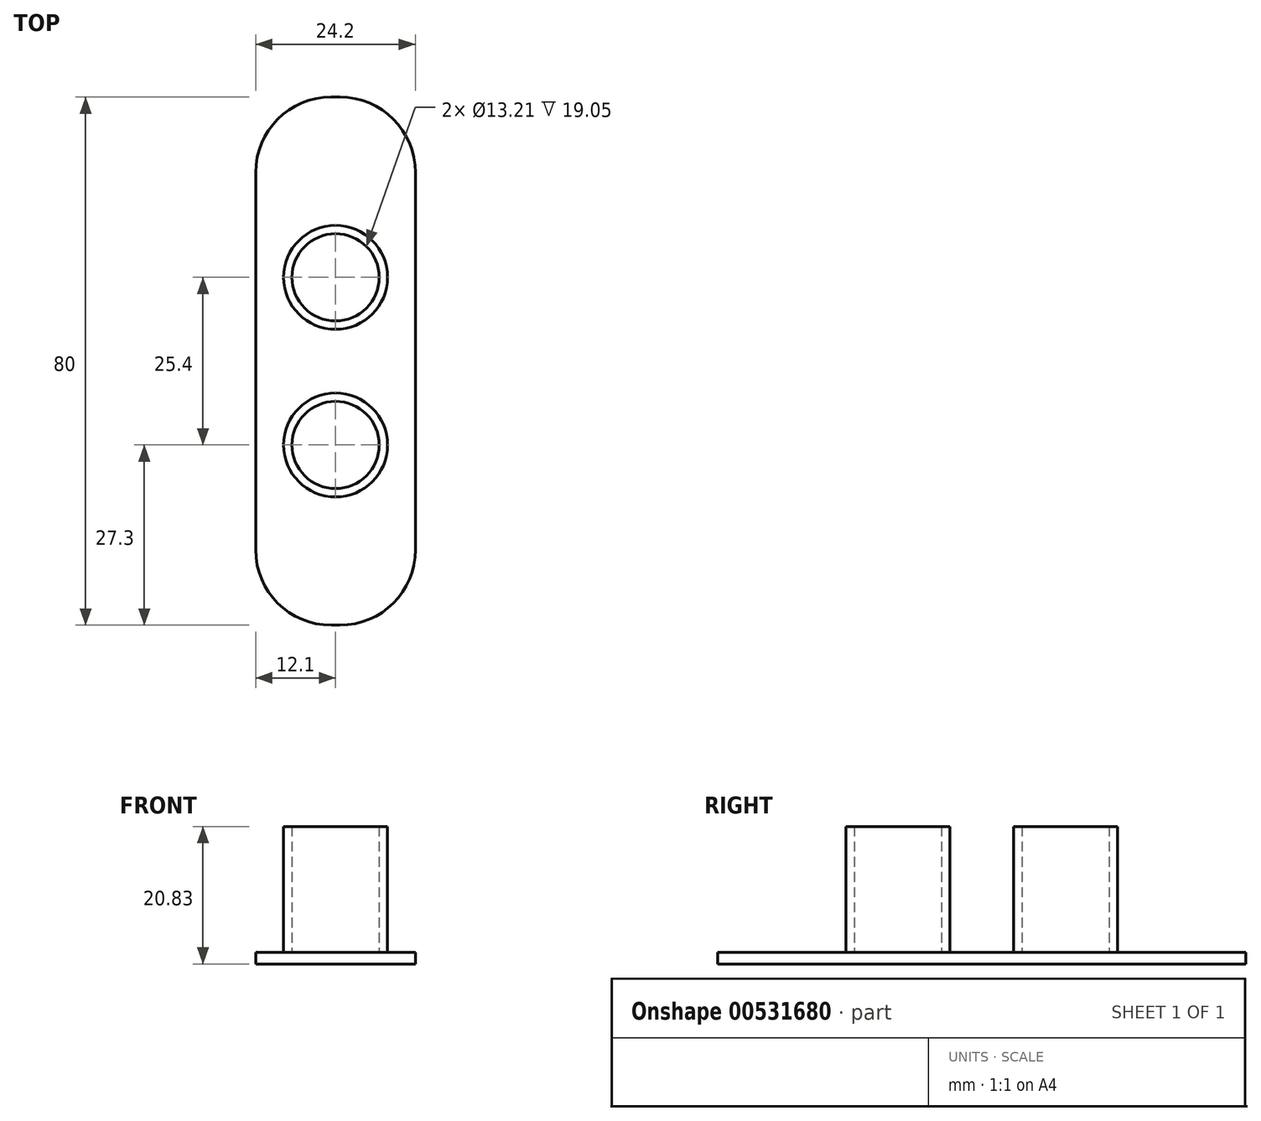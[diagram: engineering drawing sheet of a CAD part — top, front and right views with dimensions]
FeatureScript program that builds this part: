
annotation { "Feature Type Name" : "Feature", "Feature Type Description" : "" }
export const myFeature = defineFeature(function(context is Context, id is Id, definition is map)
    precondition{}
    {
        {
            var Q0;
            Q0=qCreatedBy(makeId("Top.planeOp"),FACE);
            var sketch = newSketch(context, id + "F0", { "sketchPlane" : qUnion([Q0])});
            skLineSegment(sketch, "E0.bottom", {"start": v(0.67, -40) * mm, "end": v(-0.67, -40) * mm});
            skLineSegment(sketch, "E0.top", {"start": v(0.67, 40) * mm, "end": v(-0.67, 40) * mm});
            skLineSegment(sketch, "E0.left", {"start": v(12.1, -28.58) * mm, "end": v(12.1, 28.58) * mm});
            skLineSegment(sketch, "E0.right", {"start": v(-12.1, -28.58) * mm, "end": v(-12.1, 28.58) * mm});
            skPoint(sketch, "E0.middle", {"position": v(0, 0) * mm});
            skPoint(sketch, "E1.visualSharp", {"position": v(-12.1, 40) * mm});
            skArc(sketch, "E1.filletArc", {"start": v(-0.67, 40) * mm, "mid": v(-8.76, 36.66) * mm, "end": v(-12.1, 28.58) * mm});
            skPoint(sketch, "E2.visualSharp", {"position": v(12.1, 40) * mm});
            skArc(sketch, "E2.filletArc", {"start": v(12.1, 28.58) * mm, "mid": v(8.76, 36.66) * mm, "end": v(0.67, 40) * mm});
            skPoint(sketch, "E3.visualSharp", {"position": v(12.1, -40) * mm});
            skArc(sketch, "E3.filletArc", {"start": v(0.67, -40) * mm, "mid": v(8.76, -36.66) * mm, "end": v(12.1, -28.58) * mm});
            skPoint(sketch, "E4.visualSharp", {"position": v(-12.1, -40) * mm});
            skArc(sketch, "E4.filletArc", {"start": v(-12.1, -28.58) * mm, "mid": v(-8.76, -36.66) * mm, "end": v(-0.67, -40) * mm});
            skSolve(sketch);
        }
        {
            var Q0;
            Q0=makeQuery(id+"F0.imprint","IMPRINT",FACE,{"disambiguationData":[TD([[makeQuery(id+"F0.imprint","IMPRINT",EDGE,{"derivedFrom":sQuery(id+"F0.wireOp",EDGE,"E0.bottom")}),-1.0]])]});
            extrude(context, id + "F1", {"entities" : qUnion([Q0]), "depth" : 1.78 * mm, "offsetDistance" : 25.4 * mm});
        }
        {
            var Q0;
            Q0=makeQuery(id+"F1.opExtrude","CAP_FACE",FACE,{"disambiguationData":[OSD([sQuery(id+"F0.wireOp",EDGE,"E0.bottom"),sQuery(id+"F0.wireOp",EDGE,"E0.top"),sQuery(id+"F0.wireOp",EDGE,"E0.left"),sQuery(id+"F0.wireOp",EDGE,"E0.right"),sQuery(id+"F0.wireOp",EDGE,"E1.filletArc"),sQuery(id+"F0.wireOp",EDGE,"E2.filletArc"),sQuery(id+"F0.wireOp",EDGE,"E3.filletArc"),sQuery(id+"F0.wireOp",EDGE,"E4.filletArc")])],"isStart":false});
            var sketch = newSketch(context, id + "F2", { "sketchPlane" : qUnion([Q0])});
            skLineSegment(sketch, "E5", {"start": v(0, 0) * mm, "end": v(0, 12.7) * mm});
            skLineSegment(sketch, "E6", {"start": v(0, 0) * mm, "end": v(0, -12.7) * mm});
            skCircle(sketch, "E7", {"center": v(0, 12.7) * mm, "radius": 6.6 * mm});
            skCircle(sketch, "E8", {"center": v(0, -12.7) * mm, "radius": 6.6 * mm});
            skCircle(sketch, "E9", {"center": v(0, 12.7) * mm, "radius": 7.87 * mm});
            skCircle(sketch, "E10", {"center": v(0, -12.7) * mm, "radius": 7.87 * mm});
            skSolve(sketch);
        }
        {
            var Q0;
            Q0 = qSketchRegion(id + "F2", true);
            extrude(context, id + "F3", {"entities" : qUnion([Q0]), "operationType" : NewBodyOperationType.ADD, "depth" : 19.05 * mm, "offsetDistance" : 25.4 * mm});
        }
    });
